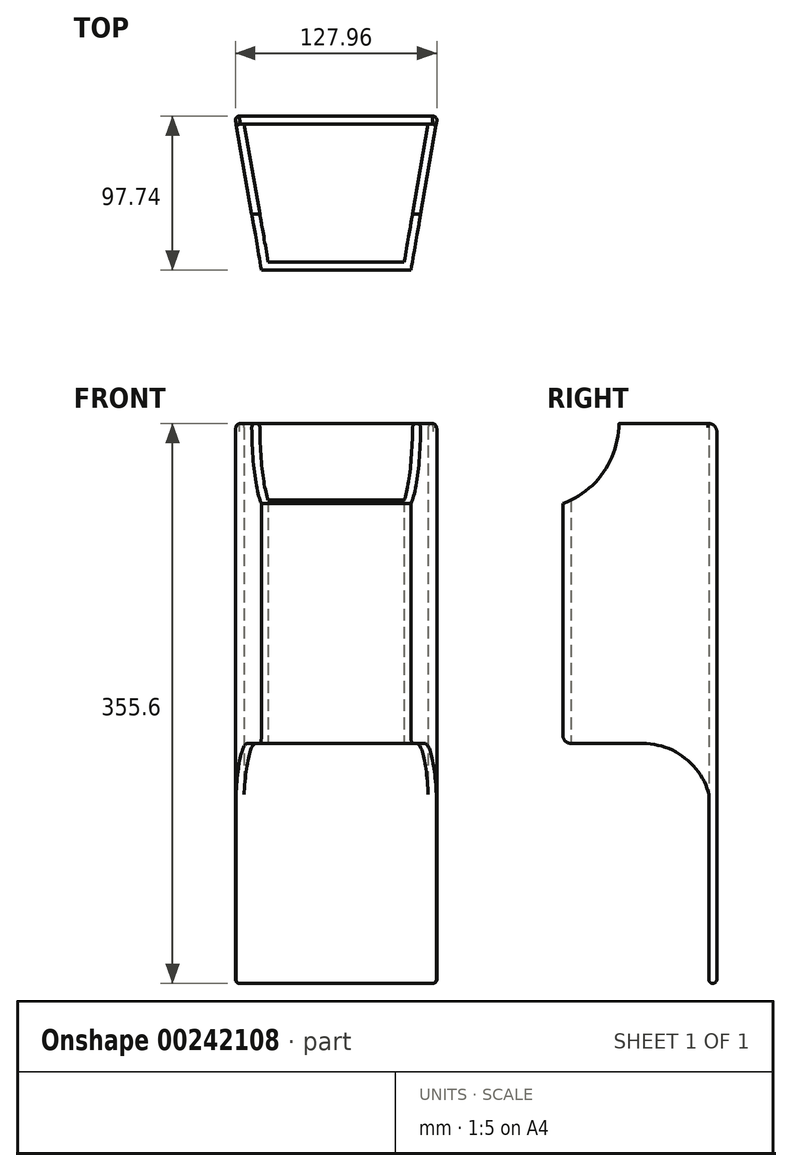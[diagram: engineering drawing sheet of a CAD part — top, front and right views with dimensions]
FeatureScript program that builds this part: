
annotation { "Feature Type Name" : "Feature", "Feature Type Description" : "" }
export const myFeature = defineFeature(function(context is Context, id is Id, definition is map)
    precondition{}
    {
        {
            var Q0;
            Q0=qCreatedBy(makeId("Top.planeOp"),FACE);
            var sketch = newSketch(context, id + "F0", { "sketchPlane" : qUnion([Q0])});
            skLineSegment(sketch, "E0", {"start": v(-58.42, 87.58) * mm, "end": v(58.42, 87.58) * mm});
            skPoint(sketch, "E1", {"position": v(0, 87.58) * mm});
            skLineSegment(sketch, "E2", {"start": v(-43.18, 0) * mm, "end": v(43.18, 0) * mm});
            skPoint(sketch, "E3", {"position": v(0, 0) * mm});
            skLineSegment(sketch, "E4", {"start": v(-43.18, 0) * mm, "end": v(-58.42, 87.58) * mm});
            skLineSegment(sketch, "E5", {"start": v(58.42, 87.58) * mm, "end": v(43.18, 0) * mm});
            skLineSegment(sketch, "E6.0", {"start": v(-64.46, 92.66) * mm, "end": v(64.46, 92.66) * mm});
            skLineSegment(sketch, "E6.1", {"start": v(-47.45, -5.08) * mm, "end": v(-64.46, 92.66) * mm});
            skLineSegment(sketch, "E6.2", {"start": v(-47.45, -5.08) * mm, "end": v(47.45, -5.08) * mm});
            skLineSegment(sketch, "E6.3", {"start": v(64.46, 92.66) * mm, "end": v(47.45, -5.08) * mm});
            skLineSegment(sketch, "E7", {"start": v(58.42, 87.58) * mm, "end": v(63.58, 87.58) * mm});
            skLineSegment(sketch, "E8", {"start": v(-58.42, 87.58) * mm, "end": v(-63.58, 87.58) * mm});
            skSolve(sketch);
        }
        {
            var Q0;
            Q0=makeQuery(id+"F0.imprint","IMPRINT",FACE,{"disambiguationData":[TD([[makeQuery(id+"F0.imprint","IMPRINT",EDGE,{"derivedFrom":sQuery(id+"F0.wireOp",EDGE,"E0")}),1.0]])]});
            extrude(context, id + "F1", {"entities" : qUnion([Q0]), "depth" : 203.2 * mm});
        }
        {
            var Q0;
            Q0=makeQuery(id+"F0.imprint","IMPRINT",FACE,{"disambiguationData":[TD([[makeQuery(id+"F0.imprint","IMPRINT",EDGE,{"derivedFrom":sQuery(id+"F0.wireOp",EDGE,"E2")}),-1.0]])]});
            extrude(context, id + "F2", {"entities" : qUnion([Q0]), "operationType" : NewBodyOperationType.ADD, "depth" : 203.2 * mm});
        }
        {
            var Q0;
            Q0=qCreatedBy(makeId("Right.planeOp"),FACE);
            var sketch = newSketch(context, id + "F3", { "sketchPlane" : qUnion([Q0])});
            skPoint(sketch, "E9", {"position": v(92.66, 203.2) * mm});
            skPoint(sketch, "E10", {"position": v(-5.08, 203.2) * mm});
            skLineSegment(sketch, "E11", {"start": v(-5.08, 203.2) * mm, "end": v(-5.08, 152.4) * mm});
            skArc(sketch, "E12", {"start": v(-5.08, 152.4) * mm, "mid": v(20.72, 172.17) * mm, "end": v(30.43, 203.2) * mm});
            skLineSegment(sketch, "E13", {"start": v(30.43, 203.2) * mm, "end": v(-5.08, 203.2) * mm});
            skSolve(sketch);
        }
        {
            var Q0;
            Q0 = qSketchRegion(id + "F3", true);
            extrude(context, id + "F4", {"entities" : qUnion([Q0]), "operationType" : NewBodyOperationType.REMOVE, "endBound" : BoundingType.SYMMETRIC, "oppositeDirection" : true, "depth" : 228.6 * mm});
        }
        {
            var Q0;
            Q0=makeQuery(id+"F0.imprint","IMPRINT",FACE,{"disambiguationData":[TD([[makeQuery(id+"F0.imprint","IMPRINT",EDGE,{"derivedFrom":sQuery(id+"F0.wireOp",EDGE,"E2")}),-1.0]])]});
            extrude(context, id + "F5", {"entities" : qUnion([Q0]), "operationType" : NewBodyOperationType.ADD, "oppositeDirection" : true, "depth" : 31.75 * mm});
        }
        {
            var Q0;
            Q0=qCreatedBy(makeId("Right.planeOp"),FACE);
            var sketch = newSketch(context, id + "F6", { "sketchPlane" : qUnion([Q0])});
            skPoint(sketch, "E14", {"position": v(87.58, -31.75) * mm});
            skArc(sketch, "E15", {"start": v(87.58, -31.75) * mm, "mid": v(72, -8.84) * mm, "end": v(45.72, 0) * mm});
            skLineSegment(sketch, "E16", {"start": v(45.72, 0) * mm, "end": v(-32.9, 0) * mm});
            skLineSegment(sketch, "E17", {"start": v(-32.9, 0) * mm, "end": v(-32.9, -53.66) * mm});
            skLineSegment(sketch, "E18", {"start": v(-32.9, -53.66) * mm, "end": v(87.58, -31.75) * mm});
            skSolve(sketch);
        }
        {
            var Q0;
            Q0=makeQuery(id+"F6.imprint","IMPRINT",FACE,{"disambiguationData":[TD([[makeQuery(id+"F6.imprint","IMPRINT",EDGE,{"derivedFrom":sQuery(id+"F6.wireOp",EDGE,"E15")}),1.0]])]});
            extrude(context, id + "F7", {"entities" : qUnion([Q0]), "operationType" : NewBodyOperationType.REMOVE, "endBound" : BoundingType.SYMMETRIC, "oppositeDirection" : true, "depth" : 203.2 * mm});
        }
        {
            var Q0;
            Q0=makeQuery(id+"F0.imprint","IMPRINT",FACE,{"disambiguationData":[TD([[makeQuery(id+"F0.imprint","IMPRINT",EDGE,{"derivedFrom":sQuery(id+"F0.wireOp",EDGE,"E0")}),1.0]])]});
            extrude(context, id + "F8", {"entities" : qUnion([Q0]), "operationType" : NewBodyOperationType.ADD, "oppositeDirection" : true, "depth" : 152.4 * mm});
        }
        {
            var Q0;
            Q0=makeQuery(id+"F1.opExtrude","CAP_EDGE",EDGE,{"disambiguationData":[OSD([sQuery(id+"F0.wireOp",EDGE,"E6.0")])],"isStart":false});
            var Q1;
            {var subQ3=sQuery(id+"F0.wireOp",EDGE,"E6.1");var subQ5=sQuery(id+"F3.wireOp",EDGE,"E12");Q1=makeQuery(id+"F4.boolean.opBoolean","COPY",EDGE,{"disambiguationData":[TD([makeQuery(id+"F1.opExtrude","SWEPT_FACE",FACE,{"disambiguationData":[OSD([subQ3])]})])],"derivedFrom":makeQuery(id+"F4.opExtrude","SWEPT_EDGE",EDGE,{"disambiguationData":[OSD([subQ5,sQuery(id+"F3.wireOp",EDGE,"E13")])]})});}
            var Q2;
            {var subQ2=sQuery(id+"F0.wireOp",EDGE,"E6.3");var subQ5=sQuery(id+"F3.wireOp",EDGE,"E12");Q2=makeQuery(id+"F4.boolean.opBoolean","COPY",EDGE,{"disambiguationData":[TD([makeQuery(id+"F1.opExtrude","SWEPT_FACE",FACE,{"disambiguationData":[OSD([subQ2])]})])],"derivedFrom":makeQuery(id+"F4.opExtrude","SWEPT_EDGE",EDGE,{"disambiguationData":[OSD([subQ5,sQuery(id+"F3.wireOp",EDGE,"E13")])]})});}
            var Q3;
            Q3=makeQuery(id+"F4.boolean.opBoolean","COPY",EDGE,{"derivedFrom":makeQuery(id+"F4.opExtrude","SWEPT_EDGE",EDGE,{"disambiguationData":[OSD([sQuery(id+"F3.wireOp",EDGE,"E11"),sQuery(id+"F3.wireOp",EDGE,"E12")])]})});
            var Q4;
            {var subQ0=sQuery(id+"F0.wireOp",EDGE,"E6.2");Q4=makeQuery(id+"F7.boolean.opBoolean","INTERSECT",EDGE,{"derivedFrom":[makeQuery(id+"F5.boolean.opBoolean","MERGE",FACE,{"derivedFrom":[makeQuery(id+"F2.opExtrude","SWEPT_FACE",FACE,{"disambiguationData":[OSD([subQ0])]}),makeQuery(id+"F5.opExtrude","SWEPT_FACE",FACE,{"disambiguationData":[OSD([subQ0])]})]}),makeQuery(id+"F7.opExtrude","SWEPT_FACE",FACE,{"disambiguationData":[OSD([sQuery(id+"F6.wireOp",EDGE,"E16")])]})]});}
            var Q5;
            {var subQ1=sQuery(id+"F0.wireOp",EDGE,"E6.1");var subQ2=sQuery(id+"F6.wireOp",EDGE,"E15");var subQ3=sQuery(id+"F6.wireOp",EDGE,"E16");Q5=makeQuery(id+"F7.boolean.opBoolean","COPY",EDGE,{"disambiguationData":[TD([makeQuery(id+"F1.opExtrude","SWEPT_FACE",FACE,{"disambiguationData":[OSD([subQ1])]})])],"derivedFrom":makeQuery(id+"F7.opExtrude","SWEPT_EDGE",EDGE,{"disambiguationData":[OSD([subQ2,subQ3])]})});}
            var Q6;
            Q6=makeQuery(id+"F7.boolean.opBoolean","MERGE",EDGE,{"derivedFrom":[makeQuery(id+"F5.opExtrude","CAP_EDGE",EDGE,{"disambiguationData":[OSD([sQuery(id+"F0.wireOp",EDGE,"E8")])],"isStart":false}),makeQuery(id+"F7.opExtrude","SWEPT_EDGE",EDGE,{"disambiguationData":[OSD([sQuery(id+"F6.wireOp",EDGE,"E15"),sQuery(id+"F6.wireOp",EDGE,"E18")])]})]});
            var Q7;
            Q7=makeQuery(id+"F7.boolean.opBoolean","MERGE",EDGE,{"derivedFrom":[makeQuery(id+"F5.opExtrude","CAP_EDGE",EDGE,{"disambiguationData":[OSD([sQuery(id+"F0.wireOp",EDGE,"E7")])],"isStart":false}),makeQuery(id+"F7.opExtrude","SWEPT_EDGE",EDGE,{"disambiguationData":[OSD([sQuery(id+"F6.wireOp",EDGE,"E15"),sQuery(id+"F6.wireOp",EDGE,"E18")])]})]});
            var Q8;
            {var subQ1=sQuery(id+"F0.wireOp",EDGE,"E6.3");var subQ2=sQuery(id+"F6.wireOp",EDGE,"E15");var subQ3=sQuery(id+"F6.wireOp",EDGE,"E16");Q8=makeQuery(id+"F7.boolean.opBoolean","COPY",EDGE,{"disambiguationData":[TD([makeQuery(id+"F1.opExtrude","SWEPT_FACE",FACE,{"disambiguationData":[OSD([subQ1])]})])],"derivedFrom":makeQuery(id+"F7.opExtrude","SWEPT_EDGE",EDGE,{"disambiguationData":[OSD([subQ2,subQ3])]})});}
            fillet(context, id + "F9", {"entities" : qUnion([Q0, Q1, Q2, Q3, Q4, Q5, Q6, Q7, Q8]), "radius" : 5.08 * mm, "tangentPropagation" : true, "allowEdgeOverflow" : false});
        }
        {
            var Q0;
            Q0=makeQuery(id+"F8.opExtrude","CAP_FACE",FACE,{"disambiguationData":[OSD([sQuery(id+"F0.wireOp",EDGE,"E0"),sQuery(id+"F0.wireOp",EDGE,"E6.0"),sQuery(id+"F0.wireOp",EDGE,"E6.1"),sQuery(id+"F0.wireOp",EDGE,"E6.3"),sQuery(id+"F0.wireOp",EDGE,"E7"),sQuery(id+"F0.wireOp",EDGE,"E8")])],"isStart":false});
            var Q1;
            Q1=makeQuery(id+"F2.opExtrude","CAP_EDGE",EDGE,{"disambiguationData":[OSD([sQuery(id+"F0.wireOp",EDGE,"E4")])],"isStart":false});
            var Q2;
            Q2=makeQuery(id+"F2.opExtrude","CAP_EDGE",EDGE,{"disambiguationData":[OSD([sQuery(id+"F0.wireOp",EDGE,"E5")])],"isStart":false});
            var Q3;
            {var subQ0=sQuery(id+"F0.wireOp",EDGE,"E6.1");Q3=makeQuery(id+"F2.boolean.opBoolean","MERGE",EDGE,{"derivedFrom":[makeQuery(id+"F1.opExtrude","CAP_EDGE",EDGE,{"disambiguationData":[OSD([subQ0])],"isStart":false}),makeQuery(id+"F2.opExtrude","CAP_EDGE",EDGE,{"disambiguationData":[OSD([subQ0])],"isStart":false})]});}
            var Q4;
            {var subQ0=sQuery(id+"F0.wireOp",EDGE,"E6.3");Q4=makeQuery(id+"F2.boolean.opBoolean","MERGE",EDGE,{"derivedFrom":[makeQuery(id+"F1.opExtrude","CAP_EDGE",EDGE,{"disambiguationData":[OSD([subQ0])],"isStart":false}),makeQuery(id+"F2.opExtrude","CAP_EDGE",EDGE,{"disambiguationData":[OSD([subQ0])],"isStart":false})]});}
            fillet(context, id + "F10", {"entities" : qUnion([Q0, Q1, Q2, Q3, Q4]), "radius" : 2.54 * mm, "tangentPropagation" : true, "allowEdgeOverflow" : false});
        }
    });
